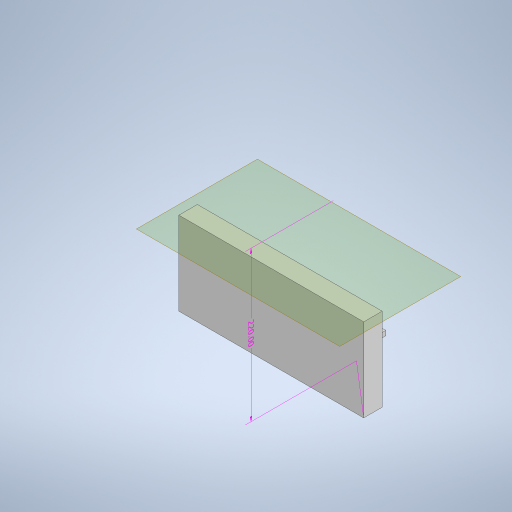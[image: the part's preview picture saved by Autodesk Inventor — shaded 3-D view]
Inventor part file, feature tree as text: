
AUTODESK INVENTOR PART (.ipt)
format: ipt  version: 2023 (Build 270158000, 158)  size: 316,416 bytes
history: native  units: mm
features: extrude x6, sketch x6, other x4, plane x3, split x1
ambient origin geometry x8: Origin, YZ Plane, XZ Plane, XY Plane, X Axis, Y Axis, Z Axis, Center Point
bodies: Body1 (feature_tree), Body2 (feature_tree)
feature tree (20):
  other  "Sólido1"
  other  "Anotaciones"
  extrude  "Extrusión1"  Depth=200.0mm
  extrude  "Extrusión2"  Depth=180.0mm
  extrude  "Extrusión3"  Depth=20.0mm
  extrude  "Extrusión4"  Depth=21.0mm
  plane  "Plano de trabajo1"
  extrude  "Extrusión6"  Depth=20.0mm
  plane  "Plano de trabajo3"
  extrude  "Extrusión7"  [1 undecoded]
  plane  "Plano de trabajo4"
  split  "Dividir1"
  sketch  "Boceto1"  dims[d0=200.0mm d1=80.0mm]
  sketch  "Boceto2"  dims[d2=130.0mm d3=0.0mm d4=180.0mm]
  sketch  "Boceto3"  dims[d5=60.0mm d6=20.0mm]
  sketch  "Boceto4"  dims[d7=60.0mm d8=0.0mm d9=21.0mm d10=43.0mm]
  sketch  "Boceto7"  dims[d11=43.0mm d12=0.0mm d13=20.0mm]
  other  "Sólido3"
  sketch  "Boceto10"  dims[d14=90.0mm d15=0.0mm d16=-90.0mm d28=20.0mm d29=20.0mm d30=30.0mm d31=30.0mm d32=20.0mm d33=35.0mm d34=35.0mm d35=69.0mm d36=5.0mm d37=0.0mm d45=1.5mm d50=10.0mm d51=0.0mm d52=10.0mm d53=89.5mm d54=90.0deg d38=3.166395mm d39=4.283575mm d40=220.0mm]
  other  "Cota lineal 1"
note: 1 required parameter value undecoded (feature->parameter linkage not recoverable at this tier; creation-order binding heuristic only, values carry confidence <= 0.55)
